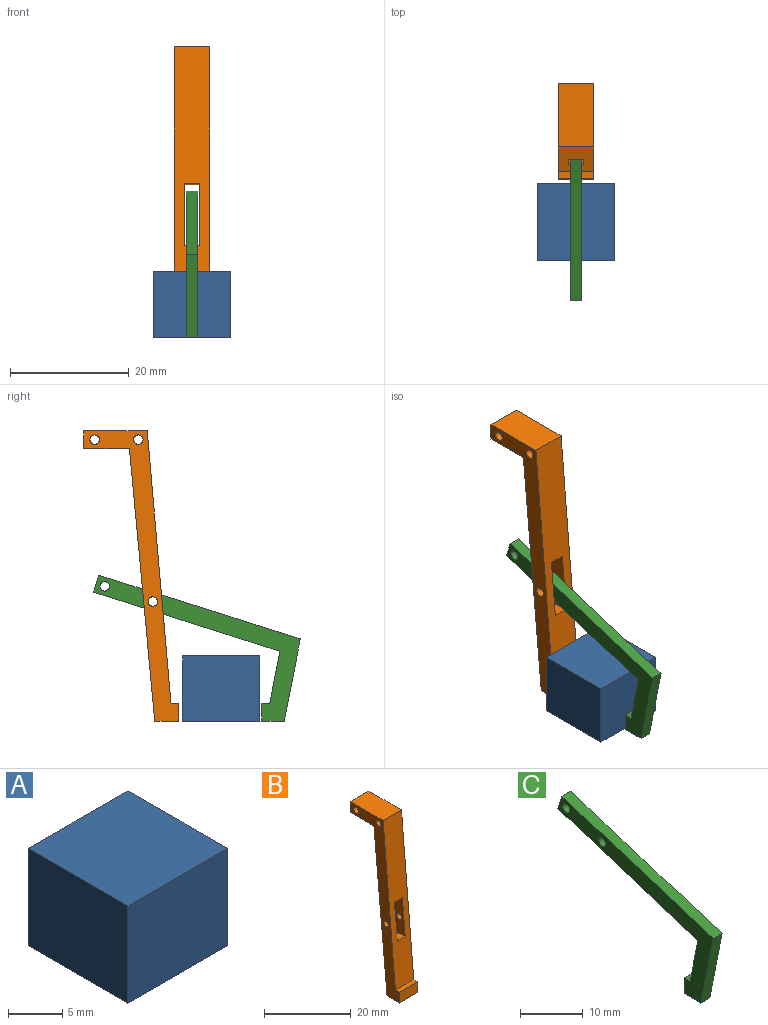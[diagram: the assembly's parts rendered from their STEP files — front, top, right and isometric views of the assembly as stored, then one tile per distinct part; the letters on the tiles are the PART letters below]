
ASSEMBLY  parts=3 mates=1
PART A: 6 faces, bbox 13x13x11 mm
  f0: plane 13x11mm, normal (0,1,0), area 143mm2, adj f1,f3,f4,f5
  f1: plane 13x11mm, normal (-1,0,0), area 143mm2, adj f0,f2,f4,f5
  f2: plane 13x11mm, normal (0,-1,0), area 143mm2, adj f1,f3,f4,f5
  f3: plane 13x11mm, normal (1,0,0), area 143mm2, adj f0,f2,f4,f5
  f4: plane 13x13mm, normal (0,0,1), area 169mm2, adj f0,f1,f2,f3
  f5: plane 13x13mm, normal (0,0,-1), area 169mm2, adj f0,f1,f2,f3
PART B: 18 faces, bbox 6x16x49 mm
  f0: cylinder r=0.8mm len=1.7mm, axis (-1,0,0), area 8.5mm2, adj f13,f17
  f1: plane 10.72x6mm, normal (0,0,1), area 64.3mm2, adj f2,f8,f12,f13
  f2: plane 46x6mm, normal (0,-1,0.09), area 249.6mm2, adj f1,f3,f12,f13,f14,f15,f16,f17
  f3: plane 6x1.3mm, normal (0,0,1), area 7.8mm2, adj f2,f4,f12,f13
  f4: plane 6x3mm, normal (0,-1,0), area 18mm2, adj f3,f5,f12,f13
  f5: plane 6x4.04mm, normal (0,0,-1), area 24.2mm2, adj f4,f6,f12,f13
  f6: plane 46x6mm, normal (0,1,-0.09), area 249.8mm2, adj f5,f7,f12,f13,f14,f15,f16,f17
  f7: plane 7.72x6mm, normal (0,0,-1), area 46.3mm2, adj f6,f8,f12,f13
  f8: plane 6x3mm, normal (0,1,0), area 18mm2, adj f1,f7,f12,f13
  f9: cylinder r=0.8mm len=6mm, axis (-1,0,0), area 30.2mm2, adj f12,f13
  f10: cylinder r=0.8mm len=6mm, axis (-1,0,0), area 30.2mm2, adj f12,f13
  f11: cylinder r=0.8mm len=1.7mm, axis (-1,0,0), area 8.5mm2, adj f12,f16
  f12: plane 49x16.04mm, normal (1,0,0), area 174.1mm2, adj f1,f2,f3,f4,f5,f6,f7,f8
  f13: plane 49x16.04mm, normal (-1,0,0), area 174.1mm2, adj f0,f1,f2,f3,f4,f5,f6,f7
  f14: plane 3.06x2.6mm, normal (0,0.09,1), area 8mm2, adj f2,f6,f16,f17
  f15: plane 3.12x2.6mm, normal (0,-0.09,-1), area 8.2mm2, adj f2,f6,f16,f17
  f16: plane 10.78x4.04mm, normal (-1,0,0), area 30.7mm2, adj f2,f6,f11,f14,f15
  f17: plane 10.78x4.04mm, normal (1,0,0), area 30.7mm2, adj f0,f2,f6,f14,f15
PART C: 12 faces, bbox 2x34.9x24.6 mm
  f0: plane 31.46x9.97mm, normal (0,0.3,-0.95), area 66mm2, adj f1,f8,f10,f11
  f1: plane 2.86x2mm, normal (0,0.95,0.3), area 6mm2, adj f0,f2,f10,f11
  f2: plane 34x10.77mm, normal (0,-0.3,0.95), area 71.3mm2, adj f1,f3,f10,f11
  f3: plane 13.87x2.74mm, normal (0,-0.98,-0.19), area 28.3mm2, adj f2,f4,f10,f11
  f4: plane 3.74x2mm, normal (0,0,-1), area 7.5mm2, adj f3,f5,f10,f11
  f5: plane 3x2mm, normal (0,1,0), area 6mm2, adj f4,f6,f10,f11
  f6: plane 2x1.3mm, normal (0,0,1), area 2.6mm2, adj f5,f8,f10,f11
  f7: cylinder r=0.8mm len=2mm, axis (-1,0,0), area 10.1mm2, adj f10,f11
  f8: plane 8.82x2mm, normal (0,0.98,0.19), area 18mm2, adj f0,f6,f10,f11
  f9: cylinder r=0.8mm len=2mm, axis (-1,0,0), area 10.1mm2, adj f10,f11
  f10: plane 34.9x24.64mm, normal (1,0,0), area 141mm2, adj f0,f1,f2,f3,f4,f5,f6,f7
  f11: plane 34.9x24.64mm, normal (-1,0,0), area 141mm2, adj f0,f1,f2,f3,f4,f5,f6,f7
PLACE A at identity
PLACE B at identity
PLACE C at identity
MATE revolute B.f0 <-> C.f7  axis (1,0,0) through (-1.3,-3.96,20.19)mm
